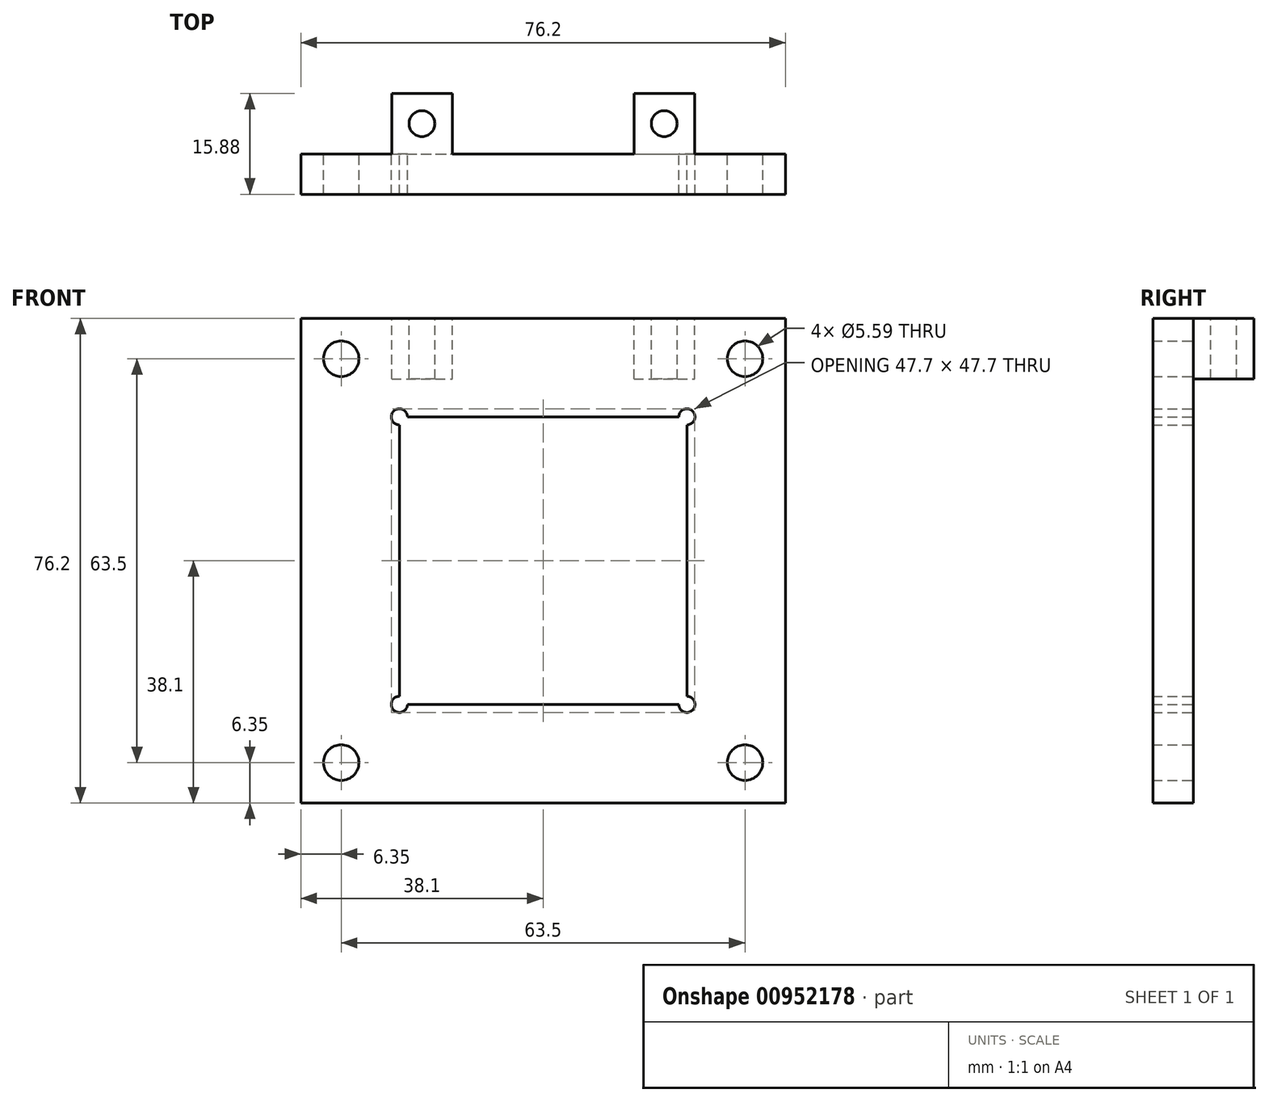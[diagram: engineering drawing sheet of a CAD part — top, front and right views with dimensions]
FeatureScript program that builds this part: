
annotation { "Feature Type Name" : "Feature", "Feature Type Description" : "" }
export const myFeature = defineFeature(function(context is Context, id is Id, definition is map)
    precondition{}
    {
        {
            var Q0;
            Q0=qCreatedBy(makeId("Front.planeOp"),FACE);
            var sketch = newSketch(context, id + "F0", { "sketchPlane" : qUnion([Q0])});
            skLineSegment(sketch, "E0.bottom", {"start": v(39.15, -38.1) * mm, "end": v(38.1, -38.1) * mm});
            skLineSegment(sketch, "E0.top", {"start": v(-38.1, 38.1) * mm, "end": v(38.1, 38.1) * mm});
            skLineSegment(sketch, "E0.right", {"start": v(38.1, -38.1) * mm, "end": v(38.1, 38.1) * mm});
            skLineSegment(sketch, "E1", {"start": v(-38.1, 38.1) * mm, "end": v(-38.1, -38.1) * mm});
            skLineSegment(sketch, "E2", {"start": v(38.1, -38.1) * mm, "end": v(-38.1, -38.1) * mm});
            skSolve(sketch);
        }
        {
            var Q0;
            Q0=qCreatedBy(makeId("Front.planeOp"),FACE);
            var sketch = newSketch(context, id + "F1", { "sketchPlane" : qUnion([Q0])});
            skLineSegment(sketch, "E3.bottom", {"start": v(-21.34, 22.6) * mm, "end": v(21.34, 22.6) * mm});
            skLineSegment(sketch, "E3.top", {"start": v(-21.34, -22.6) * mm, "end": v(21.34, -22.6) * mm});
            skLineSegment(sketch, "E3.left", {"start": v(-22.6, 21.34) * mm, "end": v(-22.6, -21.34) * mm});
            skLineSegment(sketch, "E3.right", {"start": v(22.6, 21.34) * mm, "end": v(22.6, -21.34) * mm});
            skArc(sketch, "E4", {"start": v(-21.34, 22.6) * mm, "mid": v(-23.5, 23.5) * mm, "end": v(-22.6, 21.34) * mm});
            skArc(sketch, "E5", {"start": v(22.6, 21.34) * mm, "mid": v(23.5, 23.5) * mm, "end": v(21.34, 22.6) * mm});
            skArc(sketch, "E6", {"start": v(-22.6, -21.34) * mm, "mid": v(-23.5, -23.5) * mm, "end": v(-21.34, -22.6) * mm});
            skArc(sketch, "E7", {"start": v(21.34, -22.6) * mm, "mid": v(23.5, -23.5) * mm, "end": v(22.6, -21.34) * mm});
            skSolve(sketch);
        }
        {
            var Q0;
            Q0=qCreatedBy(makeId("Front.planeOp"),FACE);
            var sketch = newSketch(context, id + "F2", { "sketchPlane" : qUnion([Q0])});
            skCircle(sketch, "E8", {"center": v(-31.75, 31.75) * mm, "radius": 2.8 * mm});
            skCircle(sketch, "E9", {"center": v(-31.75, -31.75) * mm, "radius": 2.8 * mm});
            skCircle(sketch, "E10", {"center": v(31.75, -31.75) * mm, "radius": 2.8 * mm});
            skCircle(sketch, "E11", {"center": v(31.75, 31.75) * mm, "radius": 2.8 * mm});
            skSolve(sketch);
        }
        {
            var Q0;
            Q0 = qSketchRegion(id + "F0", true);
            extrude(context, id + "F3", {"entities" : qUnion([Q0]), "depth" : 6.35 * mm, "offsetDistance" : 25.4 * mm});
        }
        {
            var Q0;
            Q0 = qSketchRegion(id + "F1", true);
            extrude(context, id + "F4", {"entities" : qUnion([Q0]), "operationType" : NewBodyOperationType.REMOVE, "endBound" : BoundingType.THROUGH_ALL, "depth" : 25.4 * mm, "offsetDistance" : 25.4 * mm});
        }
        {
            var Q0;
            Q0 = qSketchRegion(id + "F2", true);
            extrude(context, id + "F5", {"entities" : qUnion([Q0]), "operationType" : NewBodyOperationType.REMOVE, "endBound" : BoundingType.THROUGH_ALL, "depth" : 25.4 * mm, "offsetDistance" : 25.4 * mm});
        }
        {
            var Q0;
            Q0=makeQuery(id+"F3.opExtrude","SWEPT_FACE",FACE,{"disambiguationData":[OSD([sQuery(id+"F0.wireOp",EDGE,"E0.top")])]});
            var sketch = newSketch(context, id + "F6", { "sketchPlane" : qUnion([Q0])});
            skLineSegment(sketch, "E12.bottom", {"start": v(-23.81, 0) * mm, "end": v(-14.29, 0) * mm});
            skLineSegment(sketch, "E12.top", {"start": v(-23.81, 9.53) * mm, "end": v(-14.29, 9.53) * mm});
            skLineSegment(sketch, "E12.left", {"start": v(-23.81, 0) * mm, "end": v(-23.81, 9.53) * mm});
            skLineSegment(sketch, "E12.right", {"start": v(-14.29, 0) * mm, "end": v(-14.29, 9.52) * mm});
            skLineSegment(sketch, "E13.bottom", {"start": v(23.81, 0) * mm, "end": v(14.29, 0) * mm});
            skLineSegment(sketch, "E13.top", {"start": v(23.81, 9.53) * mm, "end": v(14.29, 9.52) * mm});
            skLineSegment(sketch, "E13.left", {"start": v(23.81, 0) * mm, "end": v(23.81, 9.53) * mm});
            skLineSegment(sketch, "E13.right", {"start": v(14.29, 0) * mm, "end": v(14.29, 9.52) * mm});
            skCircle(sketch, "E14", {"center": v(-19.05, 4.76) * mm, "radius": 2.03 * mm});
            skCircle(sketch, "E15", {"center": v(19.05, 4.76) * mm, "radius": 2.03 * mm});
            skSolve(sketch);
        }
        {
            var Q0;
            Q0 = qSketchRegion(id + "F6", true);
            extrude(context, id + "F7", {"entities" : qUnion([Q0]), "operationType" : NewBodyOperationType.ADD, "oppositeDirection" : true, "depth" : 9.52 * mm, "offsetDistance" : 25.4 * mm});
        }
    });
